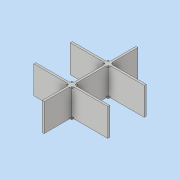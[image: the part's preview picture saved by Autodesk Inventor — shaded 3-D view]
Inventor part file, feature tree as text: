
AUTODESK INVENTOR PART (.ipt)
format: ipt  version: 2019 (Build 230136000, 136)  size: 256,512 bytes
history: native  units: mm
features: other x3, extrude x3, sketch x2, mirror x1, projected_geometry x1
ambient origin geometry x8: Origin, YZ Plane, XZ Plane, XY Plane, X Axis, Y Axis, Z Axis, Center Point
bodies: Body1 (feature_tree)
feature tree (10):
  other  "крепление-стенки"
  other  "Твердое тело1"
  sketch  "Эскиз1"
  extrude  "Выдавливание1"  Depth=150.0mm
  other  "РабПлоскость1"
  extrude  "Выдавливание2"  Depth=4.0mm
  mirror  "Зеркальное отражение1"
  extrude  "Выдавливание3"  Depth=4.0mm
  sketch  "Эскиз2"
  projected_geometry  "Спроецированная петля1"
